# Revit family: Medical_Equipment-Workstation-Midmark_Medical-6214_Procedure_Workstationp
name_source: partatom
category: Specialty Equipment
revit_build: Autodesk Revit 2018 (Build: 20190510_1515(x64)
units: mm (PartAtom-declared; Revit-internal decimal feet)

## family parameters
Always vertical = Yes
Cut with Voids When Loaded = No
OmniClass Number = 23.40.70.11.14.11
OmniClass Title = Medical Equipment
Part Type = Normal
Room Calculation Point = No
Round Connector Dimension = Use Diameter
Shared = No
Work Plane-Based = No

## types (1)
- 6214 - Base Model
    Apparent Load = 150 VA
    Assembly Code = E1020800
    Battery Life = 10 hours
    Cost = 0 $
    Description = Procedure Workstation
    Electrical Amperage = 0 A
    Electrical Frequency = 60 Hz
    Electrical Phase = 1
    Electrical Voltage = 120 V
    Manufacturer = Midmark® Medical
    Model = Midmark® Medical 6214 Procedure Workstation
    Product Documentation Link = https://www.midmark.com
    Product Page URL = https://www.midmark.com
    Product data url = https://www.bimobject.com
    URL = https://www.midmark.com
    Workstation Top Material = Wood - Midmark - Dark Walnut

## geometry (parser evidence)
native form markers: Blend x16, Sweep x24
no freeform markers — native parametric forms only
